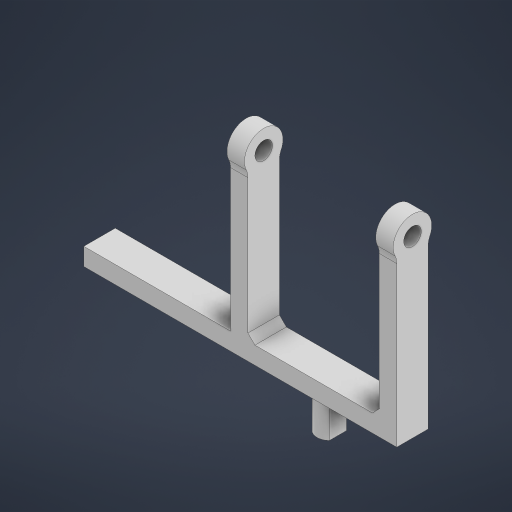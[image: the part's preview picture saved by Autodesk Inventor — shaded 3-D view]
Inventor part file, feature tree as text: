
AUTODESK INVENTOR PART (.ipt)
format: ipt  version: 2024 (Build 280153000, 153)  size: 249,344 bytes
history: native  units: mm
features: extrude x6, sketch x5, fillet x1, chamfer x1
ambient origin geometry x8: Origin, YZ Plane, XZ Plane, XY Plane, X Axis, Y Axis, Z Axis, Center Point
bodies: Body1 (feature_tree)
feature tree (13):
  extrude  "돌출4"  Depth=5.0mm
  extrude  "돌출5"  Depth=11.0mm
  extrude  "돌출6"  Depth=9.0mm
  fillet  "모깎기1"  Radius=50.0mm
  chamfer  "모따기1"  Distance=9.0mm
  sketch  "스케치7"
  extrude  "돌출7"  Depth=5.0mm TaperAngle=0.0deg
  extrude  "돌출8"  Depth=9.0mm
  extrude  "돌출9"  Depth=5.0mm
  sketch  "스케치4"
  sketch  "스케치5"
  sketch  "스케치6"
  sketch  "스케치8"
